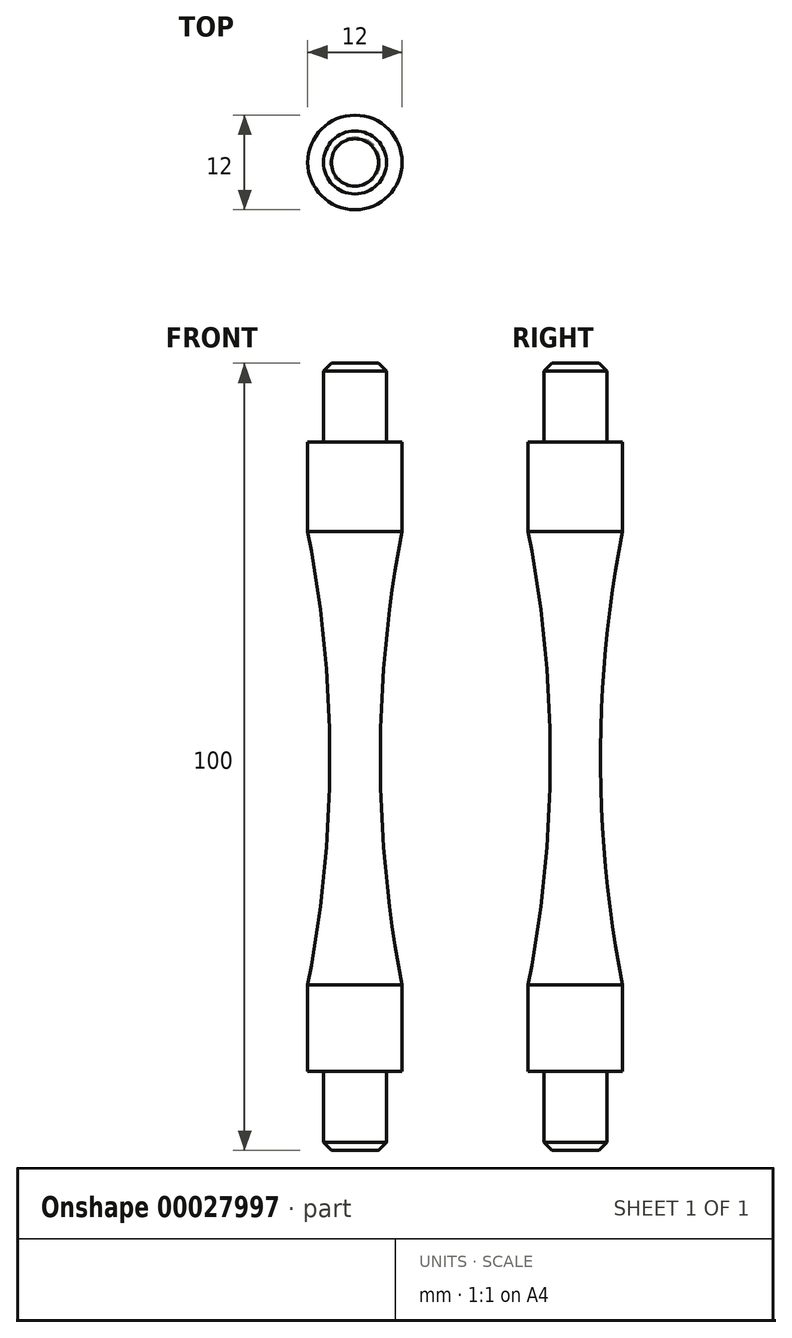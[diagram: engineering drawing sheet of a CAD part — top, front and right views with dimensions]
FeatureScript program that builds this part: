
annotation { "Feature Type Name" : "Feature", "Feature Type Description" : "" }
export const myFeature = defineFeature(function(context is Context, id is Id, definition is map)
    precondition{}
    {
        {
            var Q0;
            Q0=qCreatedBy(makeId("Top.planeOp"),FACE);
            var sketch = newSketch(context, id + "F0", { "sketchPlane" : qUnion([Q0])});
            skCircle(sketch, "E0", {"center": v(0, 0) * mm, "radius": 4 * mm});
            skSolve(sketch);
        }
        {
            var Q0;
            Q0 = qSketchRegion(id + "F0", true);
            extrude(context, id + "F1", {"entities" : qUnion([Q0]), "depth" : 10 * mm});
        }
        {
            var Q0;
            Q0=makeQuery(id+"F1.opExtrude","CAP_FACE",FACE,{"disambiguationData":[OSD([sQuery(id+"F0.wireOp",EDGE,"E0")])],"isStart":false});
            var sketch = newSketch(context, id + "F2", { "sketchPlane" : qUnion([Q0])});
            skCircle(sketch, "E1", {"center": v(0, 0) * mm, "radius": 6 * mm});
            skSolve(sketch);
        }
        {
            var Q0;
            Q0 = qSketchRegion(id + "F2", true);
            extrude(context, id + "F3", {"entities" : qUnion([Q0]), "operationType" : NewBodyOperationType.ADD, "depth" : 80 * mm});
        }
        {
            var Q0;
            Q0=makeQuery(id+"F3.opExtrude","CAP_FACE",FACE,{"disambiguationData":[OSD([sQuery(id+"F2.wireOp",EDGE,"E1")])],"isStart":false});
            var sketch = newSketch(context, id + "F4", { "sketchPlane" : qUnion([Q0])});
            skCircle(sketch, "E2", {"center": v(0, 0) * mm, "radius": 4 * mm});
            skSolve(sketch);
        }
        {
            var Q0;
            Q0 = qSketchRegion(id + "F4", true);
            extrude(context, id + "F5", {"entities" : qUnion([Q0]), "operationType" : NewBodyOperationType.ADD, "depth" : 10 * mm});
        }
        {
            var Q0;
            Q0=makeQuery(id+"F5.opExtrude","CAP_EDGE",EDGE,{"disambiguationData":[OSD([sQuery(id+"F4.wireOp",EDGE,"E2")])],"isStart":false});
            var Q1;
            Q1=makeQuery(id+"F1.opExtrude","CAP_EDGE",EDGE,{"disambiguationData":[OSD([sQuery(id+"F0.wireOp",EDGE,"E0")])],"isStart":true});
            chamfer(context, id + "F6", {"entities" : qUnion([Q0, Q1]), "width" : 1 * mm, "tangentPropagation" : true});
        }
        {
            var Q0;
            Q0=qCreatedBy(makeId("Front.planeOp"),FACE);
            var sketch = newSketch(context, id + "F7", { "sketchPlane" : qUnion([Q0])});
            skArc(sketch, "E3", {"start": v(-8.05, 12) * mm, "mid": v(-3.2, 50) * mm, "end": v(-8.15, 88) * mm});
            skLineSegment(sketch, "E4", {"start": v(-8.05, 12) * mm, "end": v(-12.89, 12) * mm});
            skLineSegment(sketch, "E5", {"start": v(-12.89, 12) * mm, "end": v(-12.89, 87.87) * mm});
            skLineSegment(sketch, "E6", {"start": v(-12.89, 87.87) * mm, "end": v(-8.15, 88) * mm});
            skSolve(sketch);
        }
        {
            var Q0;
            Q0=qCreatedBy(makeId("Front.planeOp"),FACE);
            var sketch = newSketch(context, id + "F8", { "sketchPlane" : qUnion([Q0])});
            skLineSegment(sketch, "E7", {"start": v(0, 0) * mm, "end": v(0, 88.68) * mm});
            skSolve(sketch);
        }
        {
            var Q0;
            Q0=makeQuery(id+"F7.imprint","IMPRINT",FACE,{"disambiguationData":[TD([[makeQuery(id+"F7.imprint","IMPRINT",EDGE,{"derivedFrom":sQuery(id+"F7.wireOp",EDGE,"E3")}),1.0]])]});
            var Q1;
            Q1=sQuery(id+"F8.wireOp",EDGE,"E7");
            revolve(context, id + "F9", {"operationType" : NewBodyOperationType.REMOVE, "entities" : qUnion([Q0]), "axis" : qUnion([Q1]), "revolveType" : RevolveType.FULL, "oppositeDirection" : true});
        }
    });
